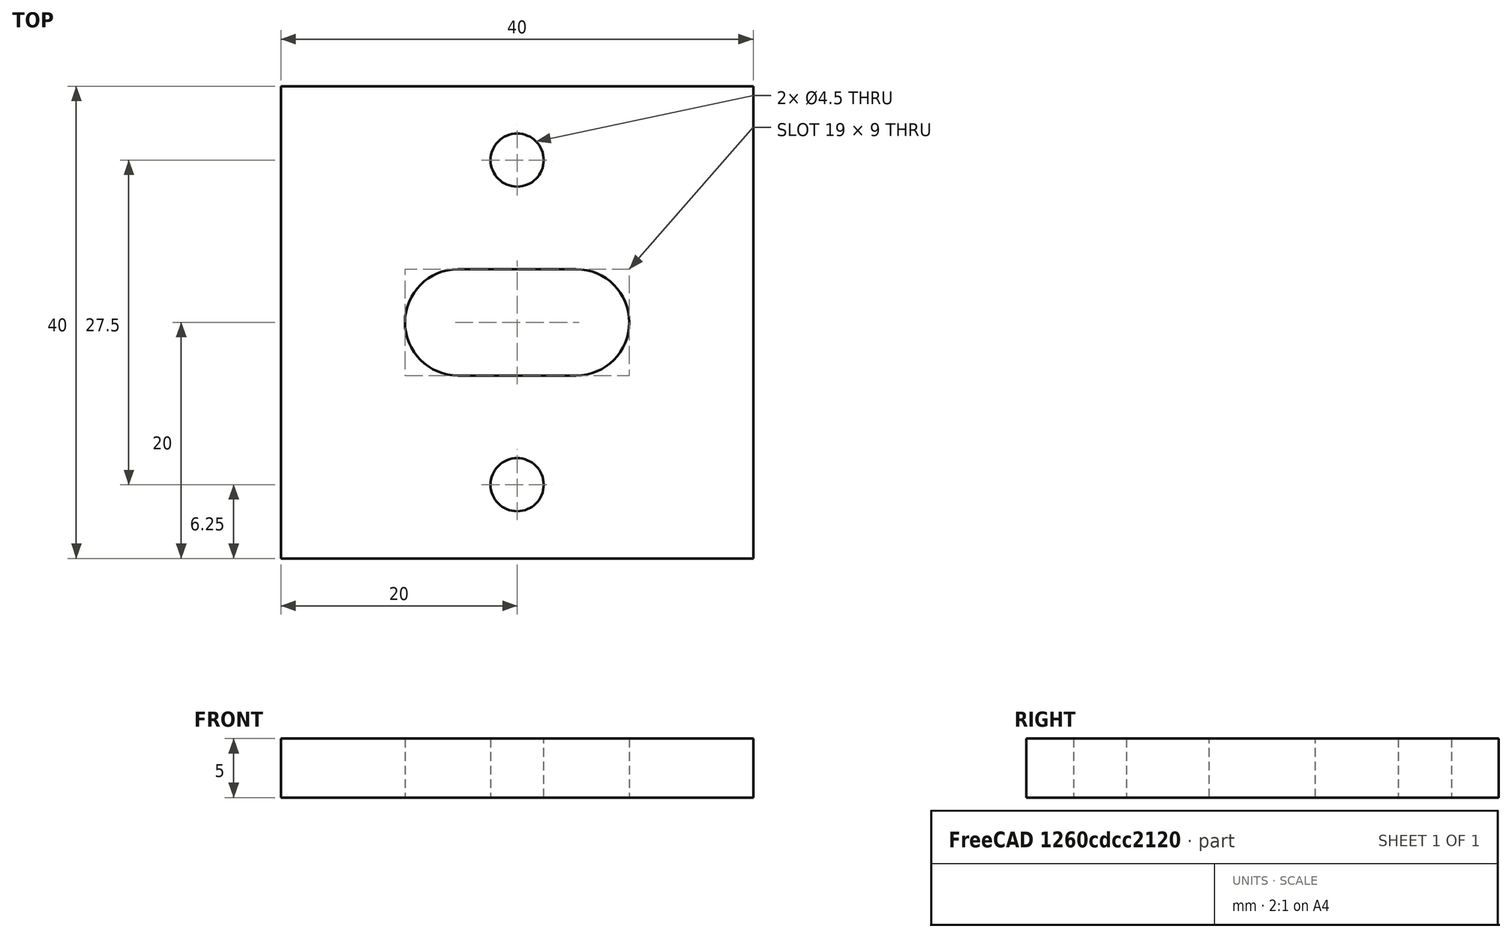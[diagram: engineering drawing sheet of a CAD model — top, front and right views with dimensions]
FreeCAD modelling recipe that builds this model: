
FCSTD DOCUMENT
Label: Z-nut-4
objects: Sketcher::SketchObject×1, PartDesign::Pad×1
note: 3 computed .brp shape members not serialized (recipe doc carries the construction recipe); baked Part::Feature solids carry a one-line shape summary decoded from their .brp

FEATURE [Sketcher::SketchObject] Sketch
  sketch-geometry (10):
    g0: LineSegment StartX=-20 StartY=20 StartZ=0 EndX=20 EndY=20 EndZ=0
    g1: LineSegment StartX=20 StartY=20 StartZ=0 EndX=20 EndY=-20 EndZ=0
    g2: LineSegment StartX=20 StartY=-20 StartZ=0 EndX=-20 EndY=-20 EndZ=0
    g3: LineSegment StartX=-20 StartY=-20 StartZ=0 EndX=-20 EndY=20 EndZ=0
    g4: ArcOfCircle CenterX=-4.99998 CenterY=0 CenterZ=0 NormalX=0 NormalY=0 NormalZ=1 Radius=4.5 StartAngle=1.5708 EndAngle=4.71239
    g5: ArcOfCircle CenterX=4.99998 CenterY=0 CenterZ=0 NormalX=0 NormalY=0 NormalZ=1 Radius=4.5 StartAngle=4.71239 EndAngle=7.85398
    g6: LineSegment StartX=-4.99998 StartY=4.5 StartZ=0 EndX=4.99998 EndY=4.5 EndZ=0
    g7: LineSegment StartX=-5 StartY=-4.5 StartZ=0 EndX=5 EndY=-4.5 EndZ=0
    g8: Circle CenterX=0 CenterY=13.75 CenterZ=0 NormalX=0 NormalY=0 NormalZ=1 Radius=2.25
    g9: Circle CenterX=0 CenterY=-13.75 CenterZ=0 NormalX=0 NormalY=0 NormalZ=1 Radius=2.25
  constraints (32):
    c: Coincident(g0,g1)
    c: Coincident(g1,g2)
    c: Coincident(g2,g3)
    c: Coincident(g3,g0)
    c: Horizontal(g0)
    c: Horizontal(g2)
    c: Vertical(g1)
    c: Vertical(g3)
    c: Symmetric(g2,g1,g-2)
    c: Symmetric(g2,g0,g-1)
    c: Distance(g2) = 40
    c: Distance(g1) = 40
    c: PointOnObject(g4,g-1)
    c: PointOnObject(g5,g-1)
    c: Equal(g4,g5)
    c: Coincident(g6,g4)
    c: Coincident(g6,g5)
    c: Horizontal(g6)
    c: Tangent(g6,g4)
    c: Coincident(g7,g4)
    c: Coincident(g7,g5)
    c: Horizontal(g7)
    c: Tangent(g7,g5)
    c: Radius(g5) = 4.5
    c: Symmetric(g4,g5,g-2)
    c: DistanceX(g4,g5) = 10
    c: PointOnObject(g8,g-2)
    c: Equal(g9,g8)
    c: Radius(g9) = 2.25
    c: PointOnObject(g9,g-2)
    c: DistanceY(g9,g8) = 27.5
    c: Symmetric(g9,g8,g-1)
FEATURE [PartDesign::Pad] Pad
  Length = 5
  Length2 = 100
  Sketch = -> Sketch
  Type = 0
